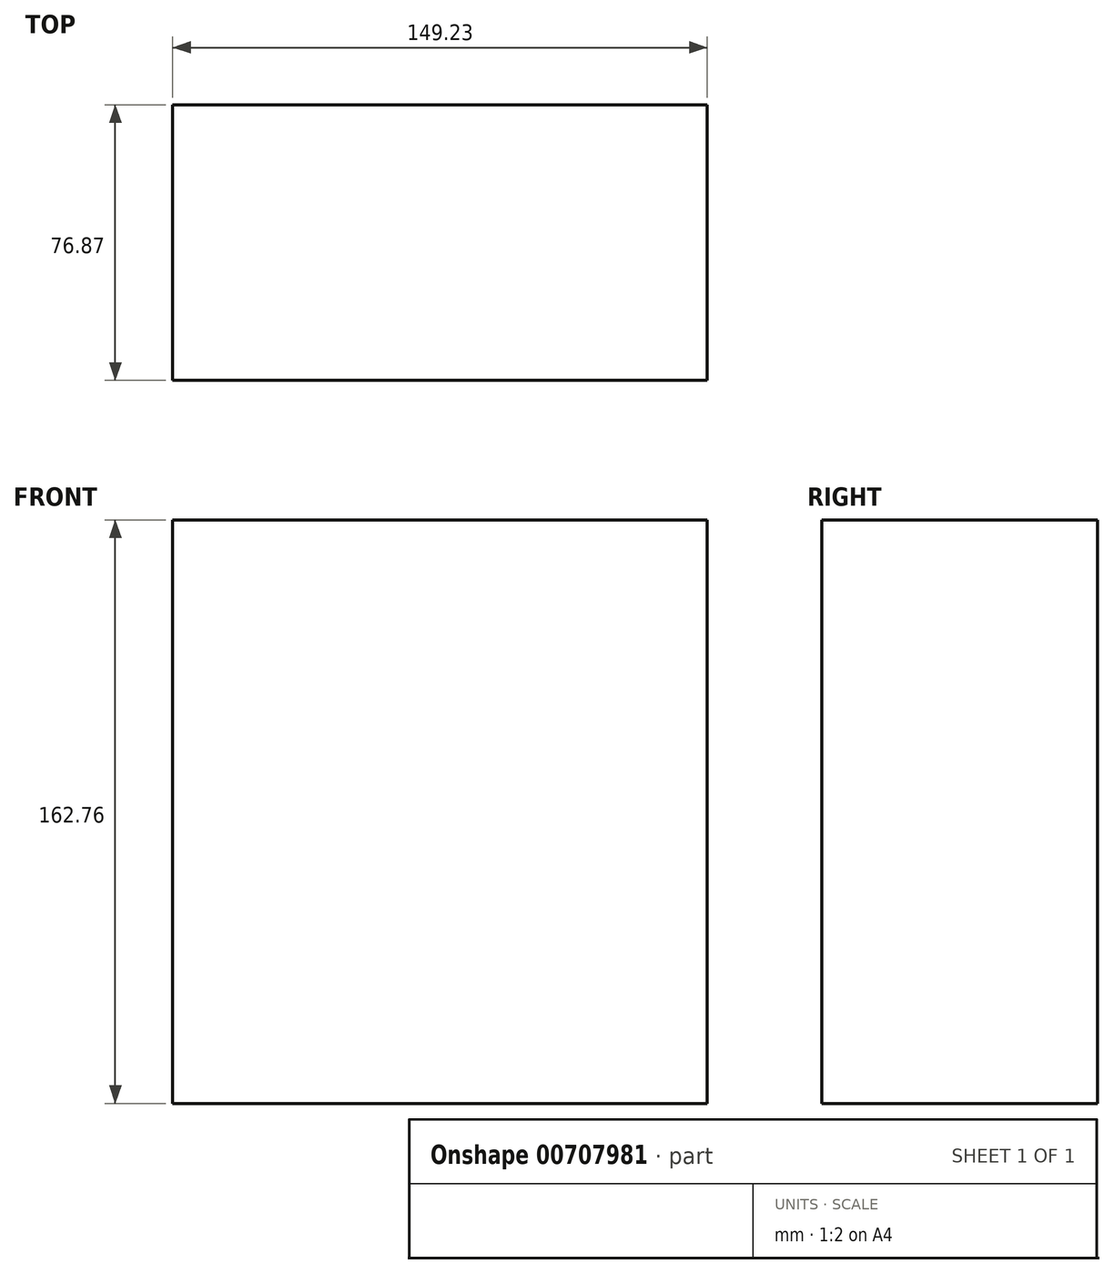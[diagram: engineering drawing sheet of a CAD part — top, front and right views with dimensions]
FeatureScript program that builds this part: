
annotation { "Feature Type Name" : "Feature", "Feature Type Description" : "" }
export const myFeature = defineFeature(function(context is Context, id is Id, definition is map)
    precondition{}
    {
        {
            var Q0;
            Q0=qCreatedBy(makeId("Top.planeOp"),FACE);
            var sketch = newSketch(context, id + "F0", { "sketchPlane" : qUnion([Q0])});
            skLineSegment(sketch, "E0.bottom", {"start": v(87.24, 23.49) * mm, "end": v(-61.99, 23.49) * mm});
            skLineSegment(sketch, "E0.top", {"start": v(87.24, -53.38) * mm, "end": v(-61.99, -53.38) * mm});
            skLineSegment(sketch, "E0.left", {"start": v(87.24, 23.49) * mm, "end": v(87.24, -53.38) * mm});
            skLineSegment(sketch, "E0.right", {"start": v(-61.99, 23.49) * mm, "end": v(-61.99, -53.38) * mm});
            skSolve(sketch);
        }
        {
            var Q0;
            Q0=makeQuery(id+"F0.imprint","IMPRINT",FACE,{"disambiguationData":[TD([[makeQuery(id+"F0.imprint","IMPRINT",EDGE,{"derivedFrom":sQuery(id+"F0.wireOp",EDGE,"E0.bottom")}),1.0]])]});
            extrude(context, id + "F1", {"entities" : qUnion([Q0]), "depth" : 162.76 * mm, "offsetDistance" : 25 * mm});
        }
    });
